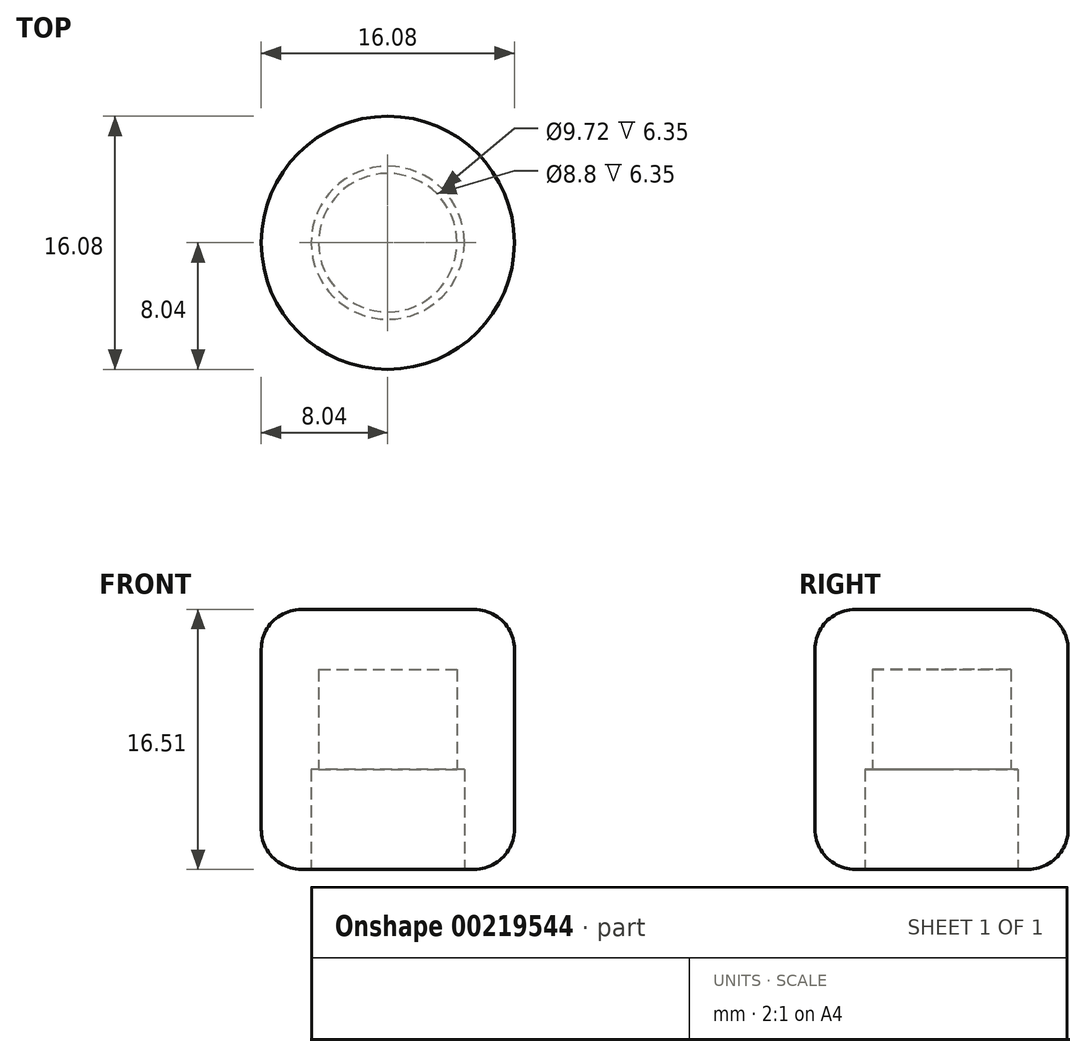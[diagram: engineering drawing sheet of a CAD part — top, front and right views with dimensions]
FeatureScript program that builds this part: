
annotation { "Feature Type Name" : "Feature", "Feature Type Description" : "" }
export const myFeature = defineFeature(function(context is Context, id is Id, definition is map)
    precondition{}
    {
        {
            var Q0;
            Q0=qCreatedBy(makeId("Top.planeOp"),FACE);
            var sketch = newSketch(context, id + "F0", { "sketchPlane" : qUnion([Q0])});
            skCircle(sketch, "E0", {"center": v(0, 0) * mm, "radius": 4.86 * mm});
            skCircle(sketch, "E1", {"center": v(0, 0) * mm, "radius": 8.04 * mm});
            skSolve(sketch);
        }
        {
            var Q0;
            Q0=makeQuery(id+"F0.imprint","IMPRINT",FACE,{"disambiguationData":[TD([[makeQuery(id+"F0.imprint","IMPRINT",EDGE,{"derivedFrom":sQuery(id+"F0.wireOp",EDGE,"E0")}),-1.0]])]});
            extrude(context, id + "F1", {"entities" : qUnion([Q0]), "depth" : 6.35 * mm});
        }
        {
            var Q0;
            Q0=makeQuery(id+"F1.opExtrude","CAP_FACE",FACE,{"disambiguationData":[OSD([sQuery(id+"F0.wireOp",EDGE,"E0"),sQuery(id+"F0.wireOp",EDGE,"E1")])],"isStart":false});
            var sketch = newSketch(context, id + "F2", { "sketchPlane" : qUnion([Q0])});
            skCircle(sketch, "E2", {"center": v(0, 0) * mm, "radius": 8.04 * mm});
            skSolve(sketch);
        }
        {
            var Q0;
            Q0 = qSketchRegion(id + "F2", true);
            extrude(context, id + "F3", {"entities" : qUnion([Q0]), "operationType" : NewBodyOperationType.ADD, "depth" : 10.16 * mm});
        }
        {
            var Q0;
            Q0=makeQuery(id+"F1.opExtrude","CAP_EDGE",EDGE,{"disambiguationData":[OSD([sQuery(id+"F0.wireOp",EDGE,"E1")])],"isStart":true});
            fillet(context, id + "F4", {"entities" : qUnion([Q0]), "radius" : 2.54 * mm, "tangentPropagation" : true, "allowEdgeOverflow" : false});
        }
        {
            var Q0;
            Q0=makeQuery(id+"F3.opExtrude","CAP_FACE",FACE,{"disambiguationData":[OSD([sQuery(id+"F2.wireOp",EDGE,"E2")])],"isStart":true});
            var sketch = newSketch(context, id + "F5", { "sketchPlane" : qUnion([Q0])});
            skCircle(sketch, "E3", {"center": v(0, 0) * mm, "radius": 4.4 * mm});
            skSolve(sketch);
        }
        {
            var Q0;
            Q0=makeQuery(id+"F5.imprint","IMPRINT",FACE,{"disambiguationData":[TD([[makeQuery(id+"F5.imprint","IMPRINT",EDGE,{"derivedFrom":sQuery(id+"F5.wireOp",EDGE,"E3")}),1.0]])]});
            extrude(context, id + "F6", {"entities" : qUnion([Q0]), "operationType" : NewBodyOperationType.REMOVE, "oppositeDirection" : true, "depth" : 6.35 * mm});
        }
        {
            var Q0;
            Q0=makeQuery(id+"F3.opExtrude","CAP_EDGE",EDGE,{"disambiguationData":[OSD([sQuery(id+"F2.wireOp",EDGE,"E2")])],"isStart":false});
            fillet(context, id + "F7", {"entities" : qUnion([Q0]), "radius" : 2.54 * mm, "tangentPropagation" : true, "allowEdgeOverflow" : false});
        }
    });
